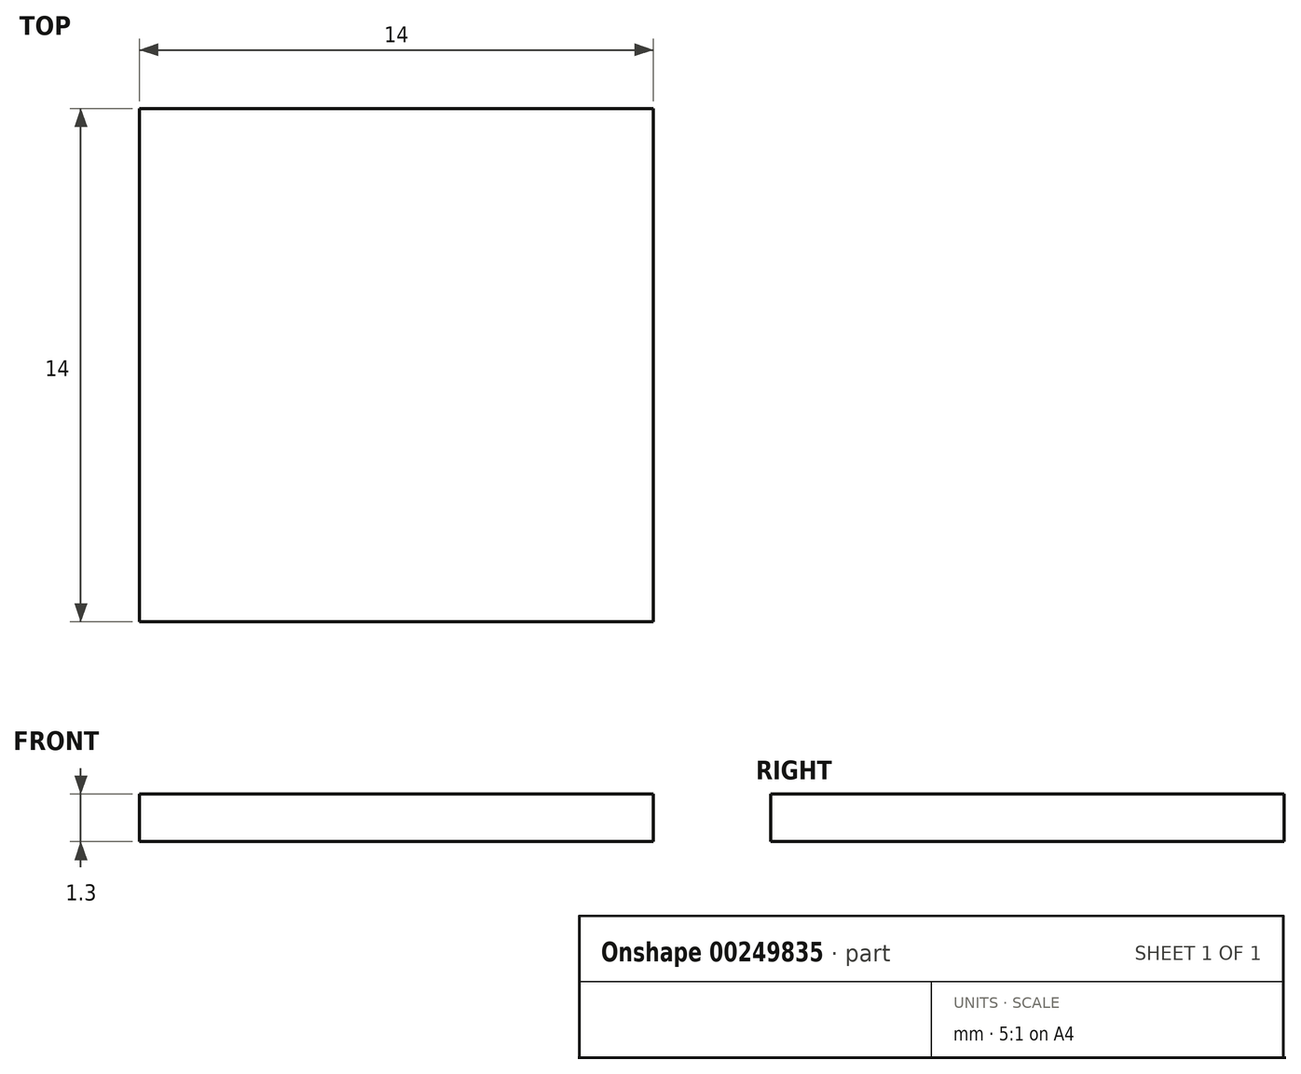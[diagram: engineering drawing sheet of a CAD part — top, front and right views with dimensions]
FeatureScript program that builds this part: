
annotation { "Feature Type Name" : "Feature", "Feature Type Description" : "" }
export const myFeature = defineFeature(function(context is Context, id is Id, definition is map)
    precondition{}
    {
        {
            var Q0;
            Q0=qCreatedBy(makeId("Top.planeOp"),FACE);
            var sketch = newSketch(context, id + "F0", { "sketchPlane" : qUnion([Q0])});
            skLineSegment(sketch, "E0.bottom", {"start": v(0, 0) * mm, "end": v(14, 0) * mm});
            skLineSegment(sketch, "E0.top", {"start": v(0, 14) * mm, "end": v(14, 14) * mm});
            skLineSegment(sketch, "E0.left", {"start": v(0, 0) * mm, "end": v(0, 14) * mm});
            skLineSegment(sketch, "E0.right", {"start": v(14, 0) * mm, "end": v(14, 14) * mm});
            skSolve(sketch);
        }
        {
            var Q0;
            Q0 = qSketchRegion(id + "F0", true);
            extrude(context, id + "F1", {"entities" : qUnion([Q0]), "depth" : 1.3 * mm});
        }
    });
